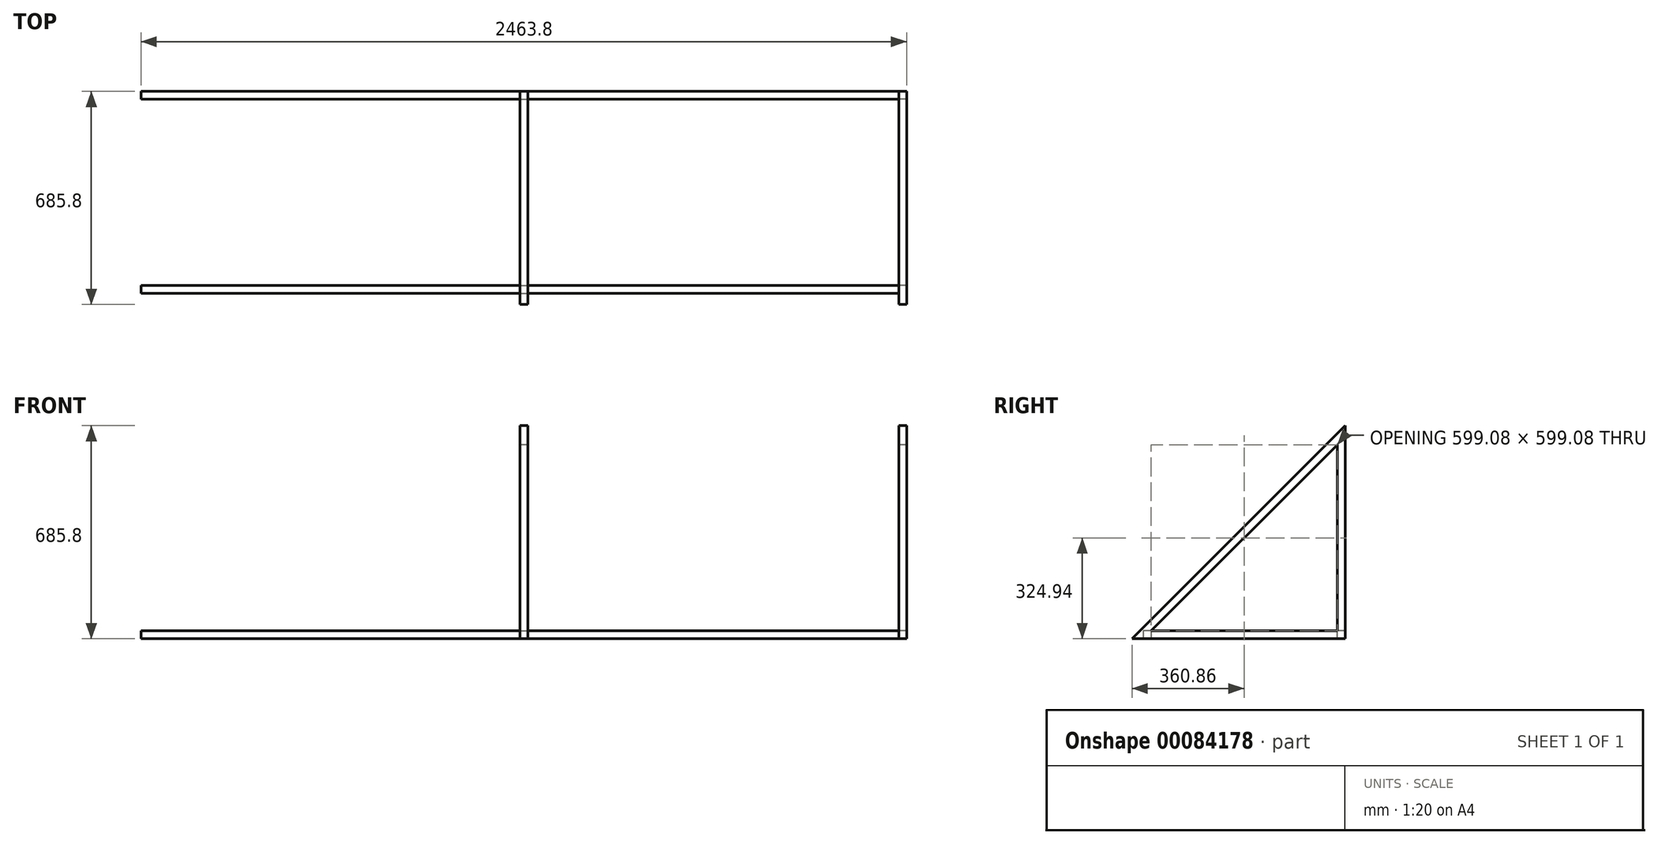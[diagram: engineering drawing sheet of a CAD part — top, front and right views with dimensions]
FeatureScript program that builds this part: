
annotation { "Feature Type Name" : "Feature", "Feature Type Description" : "" }
export const myFeature = defineFeature(function(context is Context, id is Id, definition is map)
    precondition{}
    {
        {
            var Q0;
            Q0=qCreatedBy(makeId("Right.planeOp"),FACE);
            var sketch = newSketch(context, id + "F0", { "sketchPlane" : qUnion([Q0])});
            skLineSegment(sketch, "E0", {"start": v(0, 0) * mm, "end": v(0, 685.8) * mm});
            skLineSegment(sketch, "E1", {"start": v(0, 685.8) * mm, "end": v(-685.8, 0) * mm});
            skLineSegment(sketch, "E2", {"start": v(-685.8, 0) * mm, "end": v(0, 0) * mm});
            skLineSegment(sketch, "E3", {"start": v(-25.4, 25.4) * mm, "end": v(-25.4, 624.48) * mm});
            skLineSegment(sketch, "E4", {"start": v(-25.4, 624.48) * mm, "end": v(-624.48, 25.4) * mm});
            skLineSegment(sketch, "E5", {"start": v(-624.48, 25.4) * mm, "end": v(-25.4, 25.4) * mm});
            skSolve(sketch);
        }
        {
            var Q0;
            Q0=makeQuery(id+"F0.imprint","IMPRINT",FACE,{"disambiguationData":[TD([[makeQuery(id+"F0.imprint","IMPRINT",EDGE,{"derivedFrom":sQuery(id+"F0.wireOp",EDGE,"E0")}),1.0]])]});
            extrude(context, id + "F1", {"entities" : qUnion([Q0]), "depth" : 25.4 * mm});
        }
        {
            var Q0;
            Q0=makeQuery(id+"F1.opExtrude","CAP_FACE",FACE,{"disambiguationData":[OSD([sQuery(id+"F0.wireOp",EDGE,"E0"),sQuery(id+"F0.wireOp",EDGE,"E1"),sQuery(id+"F0.wireOp",EDGE,"E2"),sQuery(id+"F0.wireOp",EDGE,"E3"),sQuery(id+"F0.wireOp",EDGE,"E4"),sQuery(id+"F0.wireOp",EDGE,"E5")])],"isStart":true});
            var sketch = newSketch(context, id + "F2", { "sketchPlane" : qUnion([Q0])});
            skLineSegment(sketch, "E6.bottom", {"start": v(0, 0) * mm, "end": v(25.4, 0) * mm});
            skLineSegment(sketch, "E6.top", {"start": v(0, 25.4) * mm, "end": v(25.4, 25.4) * mm});
            skLineSegment(sketch, "E6.left", {"start": v(0, 0) * mm, "end": v(0, 25.4) * mm});
            skLineSegment(sketch, "E6.right", {"start": v(25.4, 0) * mm, "end": v(25.4, 25.4) * mm});
            skLineSegment(sketch, "E7.bottom", {"start": v(624.48, 25.4) * mm, "end": v(649.88, 25.4) * mm});
            skLineSegment(sketch, "E7.top", {"start": v(624.48, 0) * mm, "end": v(649.88, 0) * mm});
            skLineSegment(sketch, "E7.left", {"start": v(624.48, 25.4) * mm, "end": v(624.48, 0) * mm});
            skLineSegment(sketch, "E7.right", {"start": v(649.88, 25.4) * mm, "end": v(649.88, 0) * mm});
            skSolve(sketch);
        }
        {
            var Q0;
            Q0=makeQuery(id+"F2.imprint","IMPRINT",FACE,{"disambiguationData":[TD([[makeQuery(id+"F2.imprint","IMPRINT",EDGE,{"derivedFrom":sQuery(id+"F2.wireOp",EDGE,"E6.bottom")}),-1.0]])]});
            var Q1;
            Q1=makeQuery(id+"F2.imprint","IMPRINT",FACE,{"disambiguationData":[TD([[makeQuery(id+"F2.imprint","IMPRINT",EDGE,{"derivedFrom":sQuery(id+"F2.wireOp",EDGE,"E7.bottom")}),-1.0]])]});
            extrude(context, id + "F3", {"entities" : qUnion([Q0, Q1]), "operationType" : NewBodyOperationType.ADD, "depth" : 1219.2 * mm});
        }
        {
            var Q0;
            Q0=makeQuery(id+"F1.opExtrude","SWEPT_BODY",BODY,{"disambiguationData":[OSD([sQuery(id+"F0.wireOp",EDGE,"E0"),sQuery(id+"F0.wireOp",EDGE,"E1"),sQuery(id+"F0.wireOp",EDGE,"E2"),sQuery(id+"F0.wireOp",EDGE,"E3"),sQuery(id+"F0.wireOp",EDGE,"E4"),sQuery(id+"F0.wireOp",EDGE,"E5")])]});
            var Q1;
            Q1=makeQuery(id+"F3.opExtrude","SWEPT_EDGE",EDGE,{"disambiguationData":[OSD([sQuery(id+"F0.wireOp",EDGE,"E2"),sQuery(id+"F2.wireOp",EDGE,"E7.top"),sQuery(id+"F2.wireOp",EDGE,"E7.right")])]});
            transform(context, id + "F4", {"entities" : qUnion([Q0]), "transformType" : TransformType.TRANSLATION_ENTITY, "oppositeDirectionEntity" : false, "transformLine" : qUnion([Q1]), "makeCopy" : true});
        }
    });
